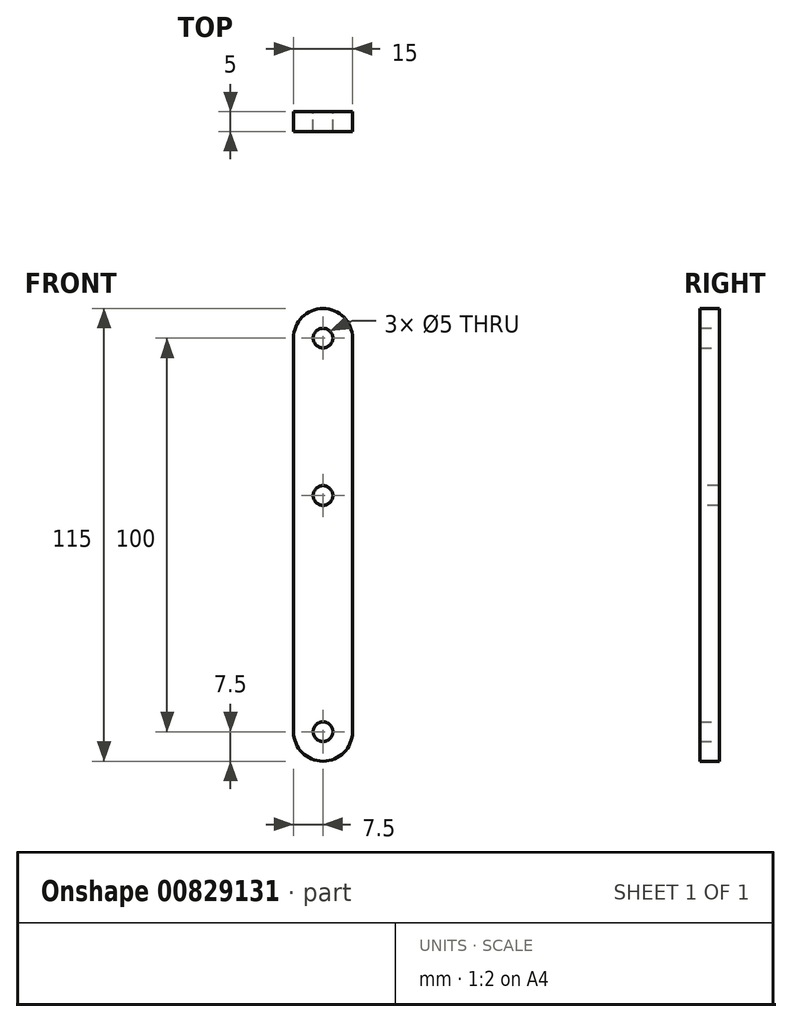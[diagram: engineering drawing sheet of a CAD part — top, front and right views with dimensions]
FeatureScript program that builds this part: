
annotation { "Feature Type Name" : "Feature", "Feature Type Description" : "" }
export const myFeature = defineFeature(function(context is Context, id is Id, definition is map)
    precondition{}
    {
        {
            var Q0;
            Q0=qCreatedBy(makeId("Front.planeOp"),FACE);
            var sketch = newSketch(context, id + "F0", { "sketchPlane" : qUnion([Q0])});
            skLineSegment(sketch, "E0.bottom", {"start": v(7.5, 50) * mm, "end": v(-7.5, 50) * mm});
            skLineSegment(sketch, "E0.top", {"start": v(7.5, -50) * mm, "end": v(-7.5, -50) * mm});
            skLineSegment(sketch, "E0.left", {"start": v(7.5, 50) * mm, "end": v(7.5, -50) * mm});
            skLineSegment(sketch, "E0.right", {"start": v(-7.5, 50) * mm, "end": v(-7.5, -50) * mm});
            skPoint(sketch, "E0.middle", {"position": v(0, 0) * mm});
            skArc(sketch, "E1", {"start": v(7.5, 50) * mm, "mid": v(0, 57.5) * mm, "end": v(-7.5, 50) * mm});
            skArc(sketch, "E2", {"start": v(-7.5, -50) * mm, "mid": v(0, -57.5) * mm, "end": v(7.5, -50) * mm});
            skCircle(sketch, "E3", {"center": v(0, 50) * mm, "radius": 2.5 * mm});
            skCircle(sketch, "E4", {"center": v(0, -50) * mm, "radius": 2.5 * mm});
            skSolve(sketch);
        }
        {
            var Q0;
            Q0 = qSketchRegion(id + "F0", true);
            extrude(context, id + "F1", {"entities" : qUnion([Q0]), "depth" : 5 * mm, "offsetDistance" : 25 * mm});
        }
        {
            var Q0;
            Q0=makeQuery(id+"F1.opExtrude","CAP_FACE",FACE,{"disambiguationData":[OSD([sQuery(id+"F0.wireOp",EDGE,"E0.left"),sQuery(id+"F0.wireOp",EDGE,"E0.right"),sQuery(id+"F0.wireOp",EDGE,"E1"),sQuery(id+"F0.wireOp",EDGE,"E2"),sQuery(id+"F0.wireOp",EDGE,"E3"),sQuery(id+"F0.wireOp",EDGE,"E4")])],"isStart":false});
            var sketch = newSketch(context, id + "F2", { "sketchPlane" : qUnion([Q0])});
            skCircle(sketch, "E5", {"center": v(0, 10) * mm, "radius": 2.5 * mm});
            skSolve(sketch);
        }
        {
            var Q0;
            Q0=makeQuery(id+"F2.imprint","IMPRINT",FACE,{"disambiguationData":[TD([[makeQuery(id+"F2.imprint","IMPRINT",EDGE,{"derivedFrom":sQuery(id+"F2.wireOp",EDGE,"E5")}),1.0]])]});
            extrude(context, id + "F3", {"entities" : qUnion([Q0]), "operationType" : NewBodyOperationType.REMOVE, "endBound" : BoundingType.THROUGH_ALL, "oppositeDirection" : true, "depth" : 25 * mm, "offsetDistance" : 25 * mm});
        }
    });
